# Revit family: Haworth_Masters_OverheadStorageUnit
name_source: partatom
category: Furniture Systems
revit_build: Autodesk Revit 2018 (Build: 20170223_1515(x64)
units: mm (PartAtom-declared; Revit-internal decimal feet)

## family parameters
Always vertical = Yes
Cut with Voids When Loaded = No
OmniClass Number = 23.40.70.14.64.21
OmniClass Title = Systems Furniture
Part Type = Normal
Room Calculation Point = No
Round Connector Dimension = Use Diameter
Shared = No
Work Plane-Based = No

## types (6) — shared parameters
Actual Depth = 16"
Arrow Offset = 6"
Assembly Code = E2020200
Base Height = 1 1/2"
Description = Haworth - Masters Overhead Storage Unit
Door Front Depth = 7/8"
Door Front Offset = 1/8"
Door Gap = 1/16"
Manufacturer = Haworth
Max Width = 108"
Min Width = 42"
Panel Thickness = 3/4"
Product Page URL = http://www.haworth.com
Revision Number = 2
Shelf Offset = 15"
Shelf Offset Bottom = 15 1/2"
Shelf Two Section = No
Size = Verify Final Dim. w/ Haworth
Sliding Left = Yes
Sliding Right = Yes
Standard Widths = 60-108 in. @ 6 in. increments
Sustainability Info = http://www.haworth.com
URL = http://www.haworth.com
Warranty = http://www.haworth.com

## per-type parameters (varying)
- 17H 96W With Glass Hinged Doors: 17in. Height=Yes; 33in. Height=No; Actual Height=16 1/2"; Actual Width=96"; Cabinet Finish=Haworth _ Wood _ Beech; Custom Size=No; Divider Center=No; Divider LR Location=32"; Divider Left Right=Yes; Door Front Height=16 1/2"; Front Finish=Haworth _ Glass _ Frosted; Glass Door=Yes; Hinged Center=Yes; Hinged Door Front Width=15 7/8"; Hinged Doors=Yes; Hinged Left Right=Yes; Shelf Finish=Haworth _ Wood _ Beech; Shelf Front Offset=1"; Shelf Three Section=No; Sliding Door=No; Sliding Door Front Width=15 7/8"; Solid Door=No; Trim Finish=Haworth _ Metal _ Brushed Aluminum; Width=96"
- 33H 96W With Glass Hinged Doors: 17in. Height=No; 33in. Height=Yes; Actual Height=32 1/2"; Actual Width=96"; Cabinet Finish=Haworth _ Wood _ Beech; Custom Size=No; Divider Center=No; Divider LR Location=32"; Divider Left Right=Yes; Door Front Height=32 1/2"; Front Finish=Haworth _ Glass _ Frosted; Glass Door=Yes; Hinged Center=Yes; Hinged Door Front Width=15 7/8"; Hinged Doors=Yes; Hinged Left Right=Yes; Shelf Finish=Haworth _ Wood _ Beech; Shelf Front Offset=1"; Shelf Three Section=Yes; Sliding Door=No; Sliding Door Front Width=15 7/8"; Solid Door=No; Trim Finish=Haworth _ Metal _ Brushed Aluminum; Width=96"
- 33H 96W With Glass Sliding Doors: 17in. Height=No; 33in. Height=Yes; Actual Height=32 1/2"; Actual Width=96"; Cabinet Finish=Haworth _ Wood _ Beech; Custom Size=No; Divider Center=No; Divider LR Location=32"; Divider Left Right=Yes; Door Front Height=32 1/2"; Front Finish=Haworth _ Glass _ Frosted; Glass Door=Yes; Hinged Center=No; Hinged Door Front Width=15 7/8"; Hinged Doors=No; Hinged Left Right=No; Shelf Finish=Haworth _ Wood _ Beech; Shelf Front Offset=2 1/2"; Shelf Three Section=Yes; Sliding Door=Yes; Sliding Door Front Width=31 7/8"; Solid Door=No; Trim Finish=Haworth _ Metal _ Brushed Aluminum; Width=96"
- 17H 96W With Glass Sliding Doors: 17in. Height=Yes; 33in. Height=No; Actual Height=16 1/2"; Actual Width=96"; Cabinet Finish=Haworth _ Wood _ Beech; Custom Size=No; Divider Center=No; Divider LR Location=32"; Divider Left Right=Yes; Door Front Height=16 1/2"; Front Finish=Haworth _ Glass _ Frosted; Glass Door=Yes; Hinged Center=No; Hinged Door Front Width=15 7/8"; Hinged Doors=No; Hinged Left Right=No; Shelf Finish=Haworth _ Wood _ Beech; Shelf Front Offset=2 1/2"; Shelf Three Section=No; Sliding Door=Yes; Sliding Door Front Width=31 7/8"; Solid Door=No; Trim Finish=Haworth _ Metal _ Brushed Aluminum; Width=96"
- 17h 42w With Glass Hinged Doors: 17in. Height=Yes; 33in. Height=No; Actual Height=16 1/2"; Actual Width=42"; Cabinet Finish=Haworth _ Wood _ Undecided _ Storage; Custom Size=Yes; Divider Center=Yes; Divider LR Location=14"; Divider Left Right=No; Door Front Height=16 1/2"; Front Finish=Haworth _ Wood _ Undecided _ Storage; Glass Door=No; Hinged Center=No; Hinged Door Front Width=20 7/8"; Hinged Doors=Yes; Hinged Left Right=Yes; Model=Haworth - Masters Overhead Storage Unit; Shelf Finish=Haworth _ Wood _ Undecided _ Storage; Shelf Front Offset=1"; Shelf Three Section=No; Sliding Door=No; Sliding Door Front Width=20 7/8"; Solid Door=Yes; Trim Finish=Haworth _ Paint _ Undecided _ Storage; Width=42"
- 17h 72w With Glass Hinged Doors: 17in. Height=Yes; 33in. Height=No; Actual Height=16 1/2"; Actual Width=72"; Cabinet Finish=Haworth _ Wood _ Undecided _ Storage; Custom Size=No; Divider Center=Yes; Divider LR Location=24"; Divider Left Right=No; Door Front Height=16 1/2"; Front Finish=Haworth _ Wood _ Undecided _ Storage; Glass Door=No; Hinged Center=No; Hinged Door Front Width=17 7/8"; Hinged Doors=Yes; Hinged Left Right=Yes; Model=Haworth - Masters Overhead Storage Unit; Shelf Finish=Haworth _ Wood _ Undecided _ Storage; Shelf Front Offset=1"; Shelf Three Section=No; Sliding Door=No; Sliding Door Front Width=17 7/8"; Solid Door=Yes; Trim Finish=Haworth _ Paint _ Undecided _ Storage; Width=72"

## geometry (parser evidence)
native form markers: Sweep x5
no freeform markers — native parametric forms only
